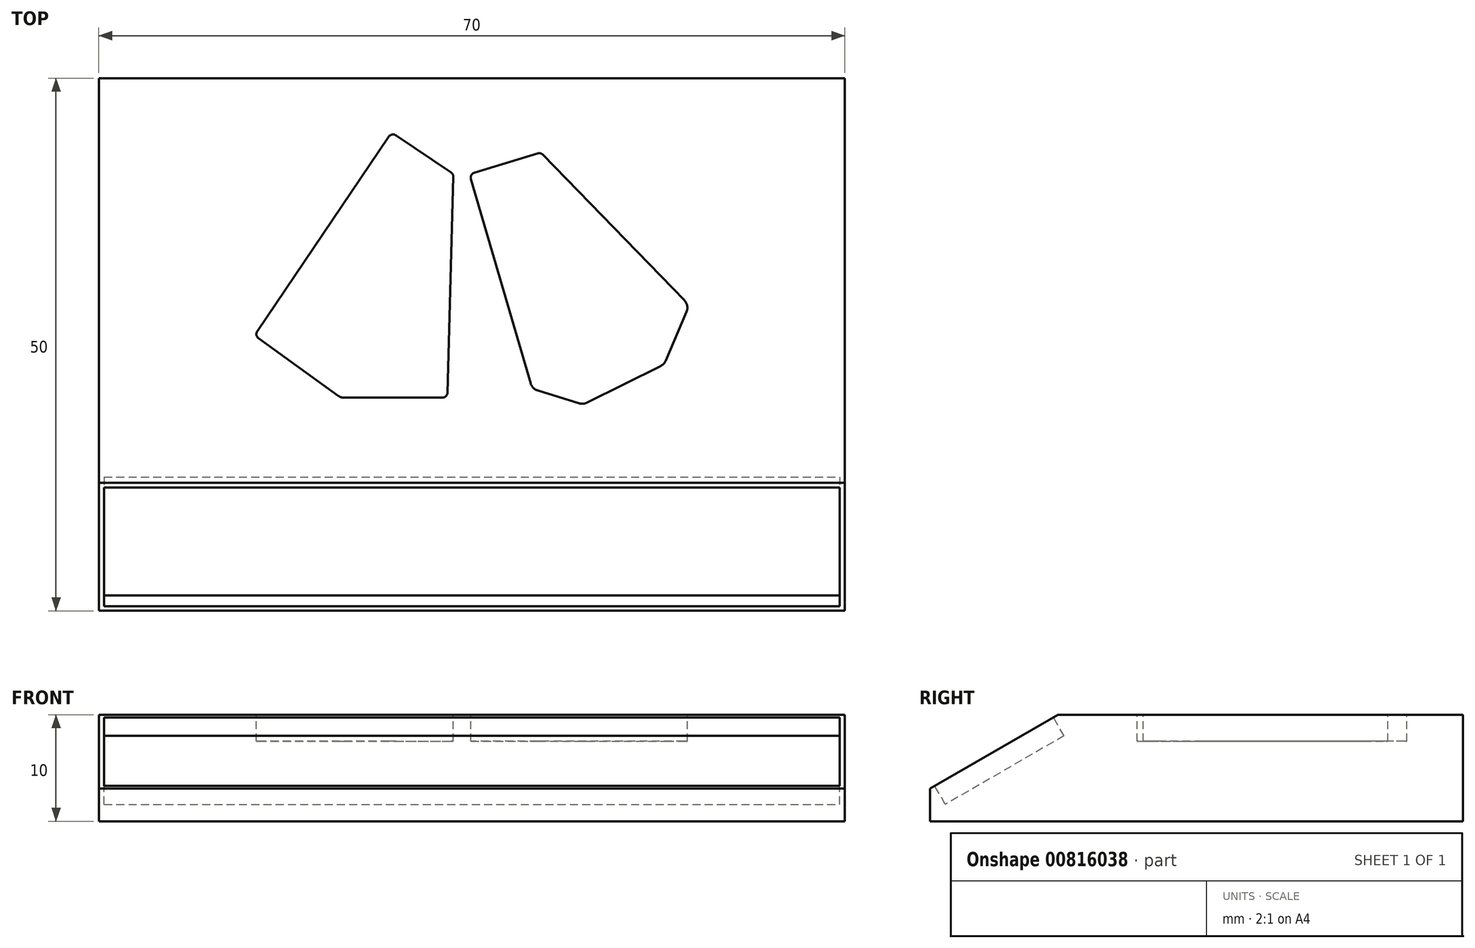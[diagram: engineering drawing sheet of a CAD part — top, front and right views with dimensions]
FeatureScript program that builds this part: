
annotation { "Feature Type Name" : "Feature", "Feature Type Description" : "" }
export const myFeature = defineFeature(function(context is Context, id is Id, definition is map)
    precondition{}
    {
        {
            var Q0;
            Q0=qCreatedBy(makeId("Top.planeOp"),FACE);
            var sketch = newSketch(context, id + "F0", { "sketchPlane" : qUnion([Q0])});
            skLineSegment(sketch, "E0.bottom", {"start": v(-29.86, 30.26) * mm, "end": v(40.14, 30.26) * mm});
            skLineSegment(sketch, "E0.top", {"start": v(-29.86, -19.74) * mm, "end": v(40.14, -19.74) * mm});
            skLineSegment(sketch, "E0.left", {"start": v(-29.86, 30.26) * mm, "end": v(-29.86, -19.74) * mm});
            skLineSegment(sketch, "E0.right", {"start": v(40.14, 30.26) * mm, "end": v(40.14, -19.74) * mm});
            skSolve(sketch);
        }
        {
            var Q0;
            Q0=makeQuery(id+"F0.imprint","IMPRINT",FACE,{"disambiguationData":[TD([[makeQuery(id+"F0.imprint","IMPRINT",EDGE,{"derivedFrom":sQuery(id+"F0.wireOp",EDGE,"E0.bottom")}),-1.0]])]});
            extrude(context, id + "F1", {"entities" : qUnion([Q0]), "depth" : 10 * mm, "offsetDistance" : 25 * mm});
        }
        {
            var Q0;
            Q0=makeQuery(id+"F1.opExtrude","CAP_EDGE",EDGE,{"disambiguationData":[OSD([sQuery(id+"F0.wireOp",EDGE,"E0.top")])],"isStart":false});
            chamfer(context, id + "F2", {"entities" : qUnion([Q0]), "chamferType" : ChamferType.OFFSET_ANGLE, "width" : 12 * mm, "oppositeDirection" : false, "angle" : 30 * degree, "tangentPropagation" : true});
        }
        {
            var Q0;
            Q0=makeQuery(id+"F1.opExtrude","CAP_FACE",FACE,{"disambiguationData":[OSD([sQuery(id+"F0.wireOp",EDGE,"E0.bottom"),sQuery(id+"F0.wireOp",EDGE,"E0.top"),sQuery(id+"F0.wireOp",EDGE,"E0.left"),sQuery(id+"F0.wireOp",EDGE,"E0.right")])],"isStart":false});
            var sketch = newSketch(context, id + "F3", { "sketchPlane" : qUnion([Q0])});
            skLineSegment(sketch, "E1", {"start": v(-2.66, 24.76) * mm, "end": v(-14.98, 6.52) * mm});
            skLineSegment(sketch, "E2", {"start": v(-1.97, 24.9) * mm, "end": v(3.2, 21.41) * mm});
            skLineSegment(sketch, "E3", {"start": v(-14.86, 5.83) * mm, "end": v(-7.4, 0.45) * mm});
            skLineSegment(sketch, "E4", {"start": v(-6.82, 0.26) * mm, "end": v(2.37, 0.26) * mm});
            skLineSegment(sketch, "E5", {"start": v(2.87, 0.75) * mm, "end": v(3.41, 20.98) * mm});
            skLineSegment(sketch, "E6", {"start": v(11.32, 23.2) * mm, "end": v(5.4, 21.4) * mm});
            skLineSegment(sketch, "E7", {"start": v(5.06, 20.78) * mm, "end": v(10.66, 1.62) * mm});
            skLineSegment(sketch, "E8", {"start": v(11.32, 0.94) * mm, "end": v(15.2, -0.26) * mm});
            skLineSegment(sketch, "E9", {"start": v(15.95, -0.2) * mm, "end": v(22.86, 3.25) * mm});
            skLineSegment(sketch, "E10", {"start": v(23.34, 3.75) * mm, "end": v(25.28, 8.32) * mm});
            skLineSegment(sketch, "E11", {"start": v(25.08, 9.41) * mm, "end": v(11.83, 23.07) * mm});
            skPoint(sketch, "E12.visualSharp", {"position": v(23.2, 3.41) * mm});
            skArc(sketch, "E12.filletArc", {"start": v(22.86, 3.25) * mm, "mid": v(23.14, 3.46) * mm, "end": v(23.34, 3.75) * mm});
            skPoint(sketch, "E13.visualSharp", {"position": v(25.54, 8.93) * mm});
            skArc(sketch, "E13.filletArc", {"start": v(25.28, 8.32) * mm, "mid": v(25.35, 8.9) * mm, "end": v(25.08, 9.41) * mm});
            skPoint(sketch, "E14.visualSharp", {"position": v(15.59, -0.38) * mm});
            skArc(sketch, "E14.filletArc", {"start": v(15.2, -0.26) * mm, "mid": v(15.58, -0.3) * mm, "end": v(15.95, -0.2) * mm});
            skPoint(sketch, "E15.visualSharp", {"position": v(10.81, 1.1) * mm});
            skArc(sketch, "E15.filletArc", {"start": v(10.66, 1.62) * mm, "mid": v(10.9, 1.2) * mm, "end": v(11.32, 0.94) * mm});
            skPoint(sketch, "E16.visualSharp", {"position": v(4.92, 21.26) * mm});
            skArc(sketch, "E16.filletArc", {"start": v(5.4, 21.4) * mm, "mid": v(5.1, 21.16) * mm, "end": v(5.06, 20.78) * mm});
            skPoint(sketch, "E17.visualSharp", {"position": v(11.62, 23.29) * mm});
            skArc(sketch, "E17.filletArc", {"start": v(11.83, 23.07) * mm, "mid": v(11.6, 23.2) * mm, "end": v(11.32, 23.2) * mm});
            skPoint(sketch, "E18.visualSharp", {"position": v(3.42, 21.26) * mm});
            skArc(sketch, "E18.filletArc", {"start": v(3.41, 20.98) * mm, "mid": v(3.35, 21.23) * mm, "end": v(3.2, 21.41) * mm});
            skPoint(sketch, "E19.visualSharp", {"position": v(-2.38, 25.17) * mm});
            skArc(sketch, "E19.filletArc", {"start": v(-1.97, 24.9) * mm, "mid": v(-2.34, 24.97) * mm, "end": v(-2.66, 24.76) * mm});
            skPoint(sketch, "E20.visualSharp", {"position": v(-15.26, 6.11) * mm});
            skArc(sketch, "E20.filletArc", {"start": v(-14.98, 6.52) * mm, "mid": v(-15.06, 6.15) * mm, "end": v(-14.86, 5.83) * mm});
            skPoint(sketch, "E21.visualSharp", {"position": v(-7.15, 0.26) * mm});
            skArc(sketch, "E21.filletArc", {"start": v(-7.4, 0.45) * mm, "mid": v(-7.13, 0.31) * mm, "end": v(-6.82, 0.26) * mm});
            skPoint(sketch, "E22.visualSharp", {"position": v(2.85, 0.26) * mm});
            skArc(sketch, "E22.filletArc", {"start": v(2.37, 0.26) * mm, "mid": v(2.72, 0.4) * mm, "end": v(2.87, 0.75) * mm});
            skSolve(sketch);
        }
        {
            var Q0;
            Q0 = qSketchRegion(id + "F3", true);
            extrude(context, id + "F4", {"entities" : qUnion([Q0]), "operationType" : NewBodyOperationType.REMOVE, "oppositeDirection" : true, "depth" : 2.5 * mm, "offsetDistance" : 25 * mm});
        }
        {
            var Q0;
            Q0=makeQuery(id+"F2.opChamfer","BLEND_FACE",FACE,{"disambiguationData":[OSD([sQuery(id+"F0.wireOp",EDGE,"E0.top")])]});
            var sketch = newSketch(context, id + "F5", { "sketchPlane" : qUnion([Q0])});
            skLineSegment(sketch, "E23.bottom", {"start": v(-29.36, -2.2) * mm, "end": v(39.64, -2.2) * mm});
            skLineSegment(sketch, "E23.top", {"start": v(-29.36, -15.06) * mm, "end": v(39.64, -15.06) * mm});
            skLineSegment(sketch, "E23.left", {"start": v(-29.36, -2.2) * mm, "end": v(-29.36, -15.06) * mm});
            skLineSegment(sketch, "E23.right", {"start": v(39.64, -2.2) * mm, "end": v(39.64, -15.06) * mm});
            skSolve(sketch);
        }
        {
            var Q0;
            Q0 = qSketchRegion(id + "F5", true);
            extrude(context, id + "F6", {"entities" : qUnion([Q0]), "operationType" : NewBodyOperationType.REMOVE, "depth" : -2 * mm, "hasOffset" : true, "offsetDistance" : -1 * mm});
        }
    });
